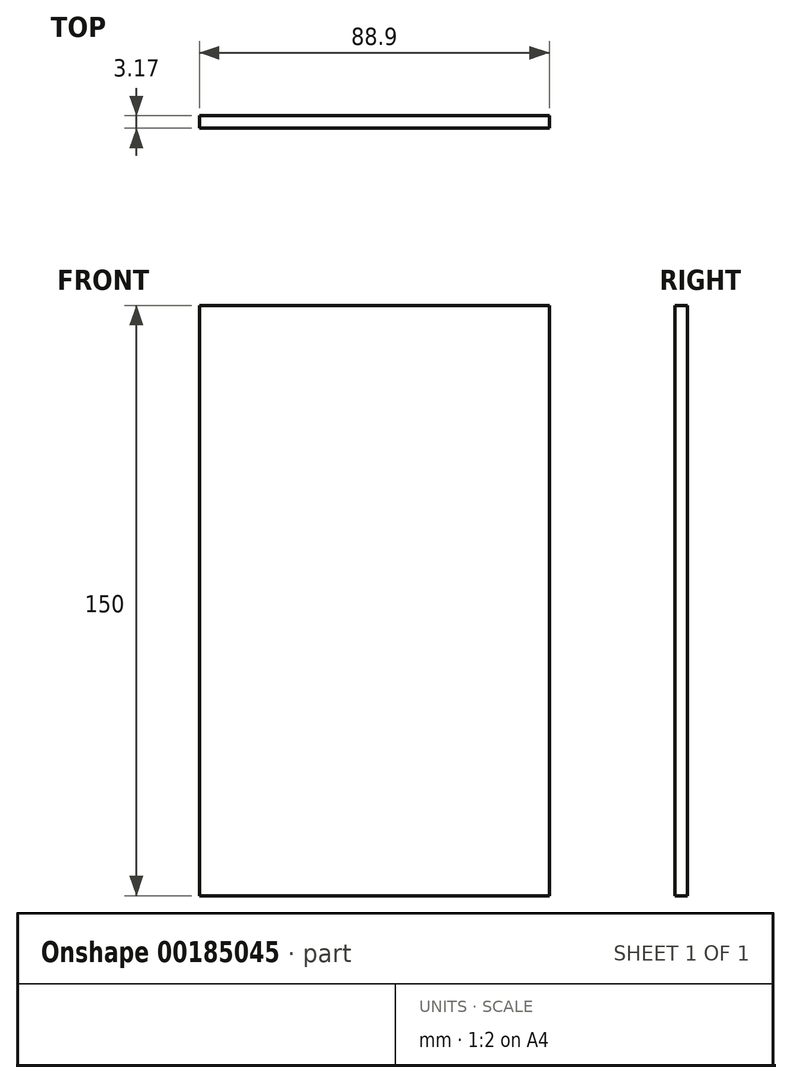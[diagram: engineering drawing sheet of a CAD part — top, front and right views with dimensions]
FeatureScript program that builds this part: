
annotation { "Feature Type Name" : "Feature", "Feature Type Description" : "" }
export const myFeature = defineFeature(function(context is Context, id is Id, definition is map)
    precondition{}
    {
        {
            var Q0;
            Q0=qCreatedBy(makeId("Front.planeOp"),FACE);
            var sketch = newSketch(context, id + "F0", { "sketchPlane" : qUnion([Q0])});
            skLineSegment(sketch, "E0.bottom", {"start": v(-44.45, 75) * mm, "end": v(44.45, 75) * mm});
            skLineSegment(sketch, "E0.top", {"start": v(-44.45, -75) * mm, "end": v(44.45, -75) * mm});
            skLineSegment(sketch, "E0.left", {"start": v(-44.45, 75) * mm, "end": v(-44.45, -75) * mm});
            skLineSegment(sketch, "E0.right", {"start": v(44.45, 75) * mm, "end": v(44.45, -75) * mm});
            skPoint(sketch, "E0.middle", {"position": v(0, 0) * mm});
            skSolve(sketch);
        }
        {
            var Q0;
            Q0=makeQuery(id+"F0.imprint","IMPRINT",FACE,{"disambiguationData":[TD([[makeQuery(id+"F0.imprint","IMPRINT",EDGE,{"derivedFrom":sQuery(id+"F0.wireOp",EDGE,"E0.bottom")}),-1.0]])]});
            extrude(context, id + "F1", {"entities" : qUnion([Q0]), "depth" : 3.17 * mm});
        }
    });
